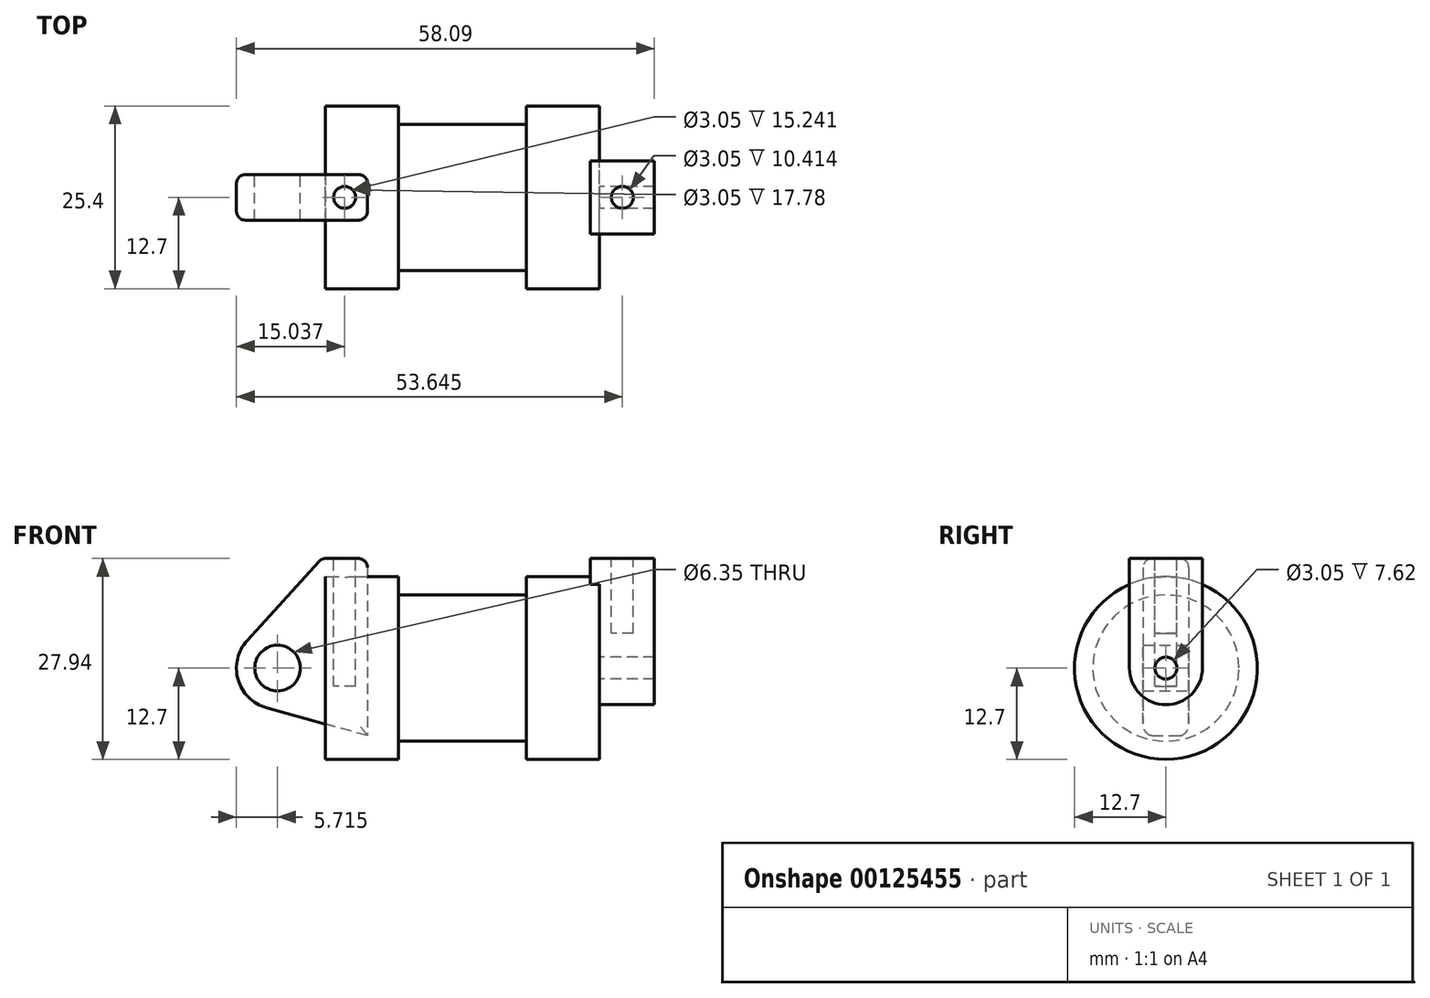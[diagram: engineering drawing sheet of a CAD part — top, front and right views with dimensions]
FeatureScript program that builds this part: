
annotation { "Feature Type Name" : "Feature", "Feature Type Description" : "" }
export const myFeature = defineFeature(function(context is Context, id is Id, definition is map)
    precondition{}
    {
        {
            var Q0;
            Q0=qCreatedBy(makeId("Front.planeOp"),FACE);
            var sketch = newSketch(context, id + "F0", { "sketchPlane" : qUnion([Q0])});
            skLineSegment(sketch, "E0", {"start": v(0, 0) * mm, "end": v(0, 12.7) * mm});
            skLineSegment(sketch, "E1", {"start": v(0, 12.7) * mm, "end": v(10.16, 12.7) * mm});
            skLineSegment(sketch, "E2", {"start": v(10.16, 12.7) * mm, "end": v(10.16, 10.16) * mm});
            skLineSegment(sketch, "E3", {"start": v(10.16, 10.16) * mm, "end": v(27.94, 10.16) * mm});
            skLineSegment(sketch, "E4", {"start": v(27.94, 10.16) * mm, "end": v(27.94, 12.7) * mm});
            skLineSegment(sketch, "E5", {"start": v(27.94, 12.7) * mm, "end": v(38.1, 12.7) * mm});
            skLineSegment(sketch, "E6", {"start": v(38.1, 12.7) * mm, "end": v(38.1, 0) * mm});
            skLineSegment(sketch, "E7", {"start": v(38.1, 0) * mm, "end": v(0, 0) * mm});
            skLineSegment(sketch, "E8", {"start": v(5.84, 15.24) * mm, "end": v(-0.5, 15.24) * mm});
            skLineSegment(sketch, "E9", {"start": v(-0.5, 15.24) * mm, "end": v(-10.88, 3.85) * mm});
            skLineSegment(sketch, "E10", {"start": v(0, 0) * mm, "end": v(-6.65, 0) * mm});
            skCircle(sketch, "E11", {"center": v(-6.65, 0) * mm, "radius": 5.72 * mm});
            skCircle(sketch, "E12", {"center": v(-6.65, 0) * mm, "radius": 3.18 * mm});
            skLineSegment(sketch, "E13", {"start": v(5.84, 15.24) * mm, "end": v(5.84, -9.4) * mm});
            skLineSegment(sketch, "E14", {"start": v(5.84, -9.4) * mm, "end": v(-8.18, -5.5) * mm});
            skSolve(sketch);
        }
        {
            var Q0;
            {var subQ3=sQuery(id+"F0.wireOp",EDGE,"E0");Q0=makeQuery(id+"F0.imprint","IMPRINT",FACE,{"disambiguationData":[TD([[makeQuery(id+"F0.imprint","IMPRINT",EDGE,{"derivedFrom":subQ3}),1.0]])]});}
            var Q1;
            {var subQ4=sQuery(id+"F0.wireOp",EDGE,"E12");Q1=makeQuery(id+"F0.imprint","IMPRINT",FACE,{"disambiguationData":[TD([[makeQuery(id+"F0.imprint","IMPRINT",EDGE,{"derivedFrom":subQ4}),-1.0]])]});}
            var Q2;
            {var subQ0=sQuery(id+"F0.wireOp",EDGE,"E14");Q2=makeQuery(id+"F0.imprint","IMPRINT",FACE,{"disambiguationData":[TD([[makeQuery(id+"F0.imprint","IMPRINT",EDGE,{"derivedFrom":subQ0}),-1.0]])]});}
            var Q3;
            {var subQ0=sQuery(id+"F0.wireOp",EDGE,"E0");Q3=makeQuery(id+"F0.imprint","IMPRINT",FACE,{"disambiguationData":[TD([[makeQuery(id+"F0.imprint","IMPRINT",EDGE,{"derivedFrom":subQ0}),-1.0]])]});}
            extrude(context, id + "F1", {"entities" : qUnion([Q0, Q1, Q2, Q3]), "endBound" : BoundingType.SYMMETRIC, "depth" : 6.35 * mm});
        }
        {
            var Q0;
            {var subQ0=sQuery(id+"F0.wireOp",EDGE,"E2");Q0=makeQuery(id+"F0.imprint","IMPRINT",FACE,{"disambiguationData":[TD([[makeQuery(id+"F0.imprint","IMPRINT",EDGE,{"derivedFrom":subQ0}),-1.0]])]});}
            var Q1;
            {var subQ0=sQuery(id+"F0.wireOp",EDGE,"E0");Q1=makeQuery(id+"F0.imprint","IMPRINT",FACE,{"disambiguationData":[TD([[makeQuery(id+"F0.imprint","IMPRINT",EDGE,{"derivedFrom":subQ0}),-1.0]])]});}
            var Q2;
            Q2=sQuery(id+"F0.wireOp",EDGE,"E7");
            revolve(context, id + "F2", {"entities" : qUnion([Q0, Q1]), "axis" : qUnion([Q2]), "revolveType" : RevolveType.FULL});
        }
        {
            var Q0;
            Q0=makeQuery(id+"F2.opRevolve","SWEPT_FACE",FACE,{"disambiguationData":[OSD([sQuery(id+"F0.wireOp",EDGE,"E6")])]});
            var sketch = newSketch(context, id + "F3", { "sketchPlane" : qUnion([Q0])});
            skCircle(sketch, "E15", {"center": v(0, 0) * mm, "radius": 1.52 * mm});
            skCircle(sketch, "E16", {"center": v(0, 0) * mm, "radius": 5.08 * mm});
            skLineSegment(sketch, "E17", {"start": v(-5.08, 0) * mm, "end": v(-5.08, 15.24) * mm});
            skLineSegment(sketch, "E18", {"start": v(5.08, 0) * mm, "end": v(5.08, 15.24) * mm});
            skLineSegment(sketch, "E19", {"start": v(-5.08, 15.24) * mm, "end": v(5.08, 15.24) * mm});
            skSolve(sketch);
        }
        {
            var Q0;
            {var subQ0=sQuery(id+"F3.wireOp",EDGE,"E19");Q0=makeQuery(id+"F3.imprint","IMPRINT",FACE,{"disambiguationData":[TD([[makeQuery(id+"F3.imprint","IMPRINT",EDGE,{"derivedFrom":subQ0}),-1.0]])]});}
            var Q1;
            {var subQ0=sQuery(id+"F3.wireOp",EDGE,"E17");var subQ1=sQuery(id+"F3.wireOp",EDGE,"E16");var subQ2=makeQuery(id+"F3.imprint","INTERSECT",VERTEX,{"derivedFrom":[subQ1,subQ0]});Q1=makeQuery(id+"F3.imprint","IMPRINT",FACE,{"disambiguationData":[TD([[makeQuery(id+"F3.imprint","IMPRINT",EDGE,{"disambiguationData":[TD([[subQ2,1.0]])],"derivedFrom":subQ1}),-1.0]])]});}
            var Q2;
            Q2=makeQuery(id+"F3.imprint","IMPRINT",FACE,{"disambiguationData":[TD([[makeQuery(id+"F3.imprint","IMPRINT",EDGE,{"derivedFrom":sQuery(id+"F3.wireOp",EDGE,"E15")}),-1.0]])]});
            extrude(context, id + "F4", {"entities" : qUnion([Q0, Q1, Q2]), "operationType" : NewBodyOperationType.ADD, "depth" : 7.62 * mm});
        }
        {
            var Q0;
            Q0 = qSketchRegion(id + "F3", true);
            extrude(context, id + "F5", {"entities" : qUnion([Q0]), "operationType" : NewBodyOperationType.ADD, "oppositeDirection" : true, "depth" : 1.27 * mm});
        }
        {
            var Q0;
            Q0=makeQuery(id+"F1.opExtrude","SWEPT_FACE",FACE,{"disambiguationData":[OSD([sQuery(id+"F0.wireOp",EDGE,"E8")])]});
            var sketch = newSketch(context, id + "F6", { "sketchPlane" : qUnion([Q0])});
            skCircle(sketch, "E20", {"center": v(2.67, 0) * mm, "radius": 1.52 * mm});
            skPoint(sketch, "E20.centerSnap0", {"position": v(2.67, -3.18) * mm});
            skLineSegment(sketch, "E21", {"start": v(-0.5, 0) * mm, "end": v(5.84, 0) * mm, "construction": true});
            skLineSegment(sketch, "E22", {"start": v(2.67, 3.18) * mm, "end": v(2.67, -3.18) * mm, "construction": true});
            skSolve(sketch);
        }
        {
            var Q0;
            Q0=makeQuery(id+"F6.imprint","IMPRINT",FACE,{"disambiguationData":[TD([[makeQuery(id+"F6.imprint","IMPRINT",EDGE,{"derivedFrom":sQuery(id+"F6.wireOp",EDGE,"E20")}),1.0]])]});
            extrude(context, id + "F7", {"entities" : qUnion([Q0]), "operationType" : NewBodyOperationType.REMOVE, "oppositeDirection" : true, "depth" : 17.78 * mm});
        }
        {
            var Q0;
            {var subQ0=sQuery(id+"F3.wireOp",EDGE,"E19");Q0=makeQuery(id+"F5.boolean.opBoolean","MERGE",FACE,{"derivedFrom":[makeQuery(id+"F4.opExtrude","SWEPT_FACE",FACE,{"disambiguationData":[OSD([subQ0])]}),makeQuery(id+"F5.opExtrude","SWEPT_FACE",FACE,{"disambiguationData":[OSD([subQ0])]})]});}
            var sketch = newSketch(context, id + "F8", { "sketchPlane" : qUnion([Q0])});
            skLineSegment(sketch, "E23", {"start": v(41.28, 5.08) * mm, "end": v(41.28, -5.08) * mm, "construction": true});
            skLineSegment(sketch, "E24", {"start": v(36.83, 0) * mm, "end": v(45.72, 0) * mm, "construction": true});
            skCircle(sketch, "E25", {"center": v(41.28, 0) * mm, "radius": 1.52 * mm});
            skSolve(sketch);
        }
        {
            var Q0;
            Q0=makeQuery(id+"F8.imprint","IMPRINT",FACE,{"disambiguationData":[TD([[makeQuery(id+"F8.imprint","IMPRINT",EDGE,{"derivedFrom":sQuery(id+"F8.wireOp",EDGE,"E25")}),1.0]])]});
            extrude(context, id + "F9", {"entities" : qUnion([Q0]), "operationType" : NewBodyOperationType.REMOVE, "oppositeDirection" : true, "depth" : 10.4 * mm});
        }
        {
            var Q0;
            Q0=makeQuery(id+"F2.opRevolve","SWEPT_EDGE",EDGE,{"disambiguationData":[OSD([sQuery(id+"F0.wireOp",EDGE,"E2"),sQuery(id+"F0.wireOp",EDGE,"E3")])]});
            var Q1;
            Q1=makeQuery(id+"F2.opRevolve","SWEPT_EDGE",EDGE,{"disambiguationData":[OSD([sQuery(id+"F0.wireOp",EDGE,"E1"),sQuery(id+"F0.wireOp",EDGE,"E2")])]});
            var Q2;
            Q2=makeQuery(id+"F1.opExtrude","CAP_EDGE",EDGE,{"disambiguationData":[OSD([sQuery(id+"F0.wireOp",EDGE,"E13")])],"isStart":false});
            var Q3;
            Q3=makeQuery(id+"F1.opExtrude","CAP_EDGE",EDGE,{"disambiguationData":[OSD([sQuery(id+"F0.wireOp",EDGE,"E8")])],"isStart":false});
            var Q4;
            Q4=makeQuery(id+"F1.opExtrude","SWEPT_EDGE",EDGE,{"disambiguationData":[OSD([sQuery(id+"F0.wireOp",EDGE,"E8"),sQuery(id+"F0.wireOp",EDGE,"E13")])]});
            var Q5;
            Q5=makeQuery(id+"F1.opExtrude","CAP_EDGE",EDGE,{"disambiguationData":[OSD([sQuery(id+"F0.wireOp",EDGE,"E9")])],"isStart":false});
            var Q6;
            Q6=makeQuery(id+"F2.opRevolve","SWEPT_EDGE",EDGE,{"disambiguationData":[OSD([sQuery(id+"F0.wireOp",EDGE,"E0"),sQuery(id+"F0.wireOp",EDGE,"E1")])]});
            var Q7;
            Q7=makeQuery(id+"F1.opExtrude","CAP_EDGE",EDGE,{"disambiguationData":[OSD([sQuery(id+"F0.wireOp",EDGE,"E9")])],"isStart":true});
            var Q8;
            Q8=makeQuery(id+"F1.opExtrude","SWEPT_EDGE",EDGE,{"disambiguationData":[OSD([sQuery(id+"F0.wireOp",EDGE,"E8"),sQuery(id+"F0.wireOp",EDGE,"E9")])]});
            var Q9;
            Q9=makeQuery(id+"F1.opExtrude","CAP_EDGE",EDGE,{"disambiguationData":[OSD([sQuery(id+"F0.wireOp",EDGE,"E8")])],"isStart":true});
            var Q10;
            Q10=makeQuery(id+"F1.opExtrude","CAP_EDGE",EDGE,{"disambiguationData":[OSD([sQuery(id+"F0.wireOp",EDGE,"E13")])],"isStart":true});
            var Q11;
            Q11=makeQuery(id+"F1.opExtrude","CAP_EDGE",EDGE,{"disambiguationData":[OSD([sQuery(id+"F0.wireOp",EDGE,"E11")])],"isStart":true});
            var Q12;
            Q12=makeQuery(id+"F1.opExtrude","CAP_EDGE",EDGE,{"disambiguationData":[OSD([sQuery(id+"F0.wireOp",EDGE,"E14")])],"isStart":true});
            var Q13;
            Q13=makeQuery(id+"F1.opExtrude","CAP_EDGE",EDGE,{"disambiguationData":[OSD([sQuery(id+"F0.wireOp",EDGE,"E11")])],"isStart":false});
            var Q14;
            Q14=makeQuery(id+"F2.opRevolve","SWEPT_EDGE",EDGE,{"disambiguationData":[OSD([sQuery(id+"F0.wireOp",EDGE,"E4"),sQuery(id+"F0.wireOp",EDGE,"E5")])]});
            var Q15;
            Q15=makeQuery(id+"F2.opRevolve","SWEPT_EDGE",EDGE,{"disambiguationData":[OSD([sQuery(id+"F0.wireOp",EDGE,"E3"),sQuery(id+"F0.wireOp",EDGE,"E4")])]});
            var Q16;
            Q16=makeQuery(id+"F5.opExtrude","CAP_EDGE",EDGE,{"disambiguationData":[OSD([sQuery(id+"F3.wireOp",EDGE,"E17")])],"isStart":false});
            var Q17;
            Q17=makeQuery(id+"F4.opExtrude","CAP_EDGE",EDGE,{"disambiguationData":[OSD([sQuery(id+"F3.wireOp",EDGE,"E19")])],"isStart":false});
            var Q18;
            {var subQ0=sQuery(id+"F3.wireOp",EDGE,"E19");var subQ1=sQuery(id+"F3.wireOp",EDGE,"E17");Q18=makeQuery(id+"F5.boolean.opBoolean","MERGE",EDGE,{"derivedFrom":[makeQuery(id+"F4.opExtrude","SWEPT_EDGE",EDGE,{"disambiguationData":[OSD([subQ1,subQ0])]}),makeQuery(id+"F5.opExtrude","SWEPT_EDGE",EDGE,{"disambiguationData":[OSD([subQ1,subQ0])]})]});}
            var Q19;
            Q19=makeQuery(id+"F4.opExtrude","CAP_EDGE",EDGE,{"disambiguationData":[OSD([sQuery(id+"F3.wireOp",EDGE,"E17")])],"isStart":false});
            var Q20;
            {var subQ0=sQuery(id+"F3.wireOp",EDGE,"E19");var subQ1=sQuery(id+"F3.wireOp",EDGE,"E18");Q20=makeQuery(id+"F5.boolean.opBoolean","MERGE",EDGE,{"derivedFrom":[makeQuery(id+"F4.opExtrude","SWEPT_EDGE",EDGE,{"disambiguationData":[OSD([subQ1,subQ0])]}),makeQuery(id+"F5.opExtrude","SWEPT_EDGE",EDGE,{"disambiguationData":[OSD([subQ1,subQ0])]})]});}
            var Q21;
            Q21=makeQuery(id+"F5.opExtrude","CAP_EDGE",EDGE,{"disambiguationData":[OSD([sQuery(id+"F3.wireOp",EDGE,"E19")])],"isStart":false});
            var Q22;
            Q22=makeQuery(id+"F4.boolean.opBoolean","SPLIT",EDGE,{"disambiguationData":[OD(1.0)],"derivedFrom":makeQuery(id+"F2.opRevolve","SWEPT_EDGE",EDGE,{"disambiguationData":[OSD([sQuery(id+"F0.wireOp",EDGE,"E5"),sQuery(id+"F0.wireOp",EDGE,"E6")])]})});
            var Q23;
            {var subQ0=sQuery(id+"F3.wireOp",EDGE,"E16");var subQ1=sQuery(id+"F3.wireOp",EDGE,"E18");Q23=makeQuery(id+"F4.boolean.opBoolean","SPLIT",EDGE,{"disambiguationData":[TD([makeQuery(id+"F4.opExtrude","SWEPT_FACE",FACE,{"disambiguationData":[OSD([subQ0])]})])],"derivedFrom":makeQuery(id+"F4.opExtrude","CAP_EDGE",EDGE,{"disambiguationData":[OSD([subQ1])],"isStart":true})});}
            var Q24;
            Q24=makeQuery(id+"F4.opExtrude","CAP_EDGE",EDGE,{"disambiguationData":[OSD([sQuery(id+"F3.wireOp",EDGE,"E18")])],"isStart":false});
            var Q25;
            Q25=makeQuery(id+"F5.opExtrude","CAP_EDGE",EDGE,{"disambiguationData":[OSD([sQuery(id+"F3.wireOp",EDGE,"E18")])],"isStart":false});
            var Q26;
            Q26=makeQuery(id+"F4.opExtrude","CAP_EDGE",EDGE,{"disambiguationData":[OSD([sQuery(id+"F3.wireOp",EDGE,"E16")])],"isStart":false});
            fillet(context, id + "F10", {"entities" : qUnion([Q0, Q1, Q2, Q3, Q4, Q5, Q6, Q7, Q8, Q9, Q10, Q11, Q12, Q13, Q14, Q15, Q16, Q17, Q18, Q19, Q20, Q21, Q22, Q23, Q24, Q25, Q26]), "radius" : 1.27 * mm, "tangentPropagation" : true, "allowEdgeOverflow" : false});
        }
    });
